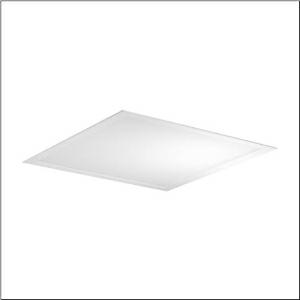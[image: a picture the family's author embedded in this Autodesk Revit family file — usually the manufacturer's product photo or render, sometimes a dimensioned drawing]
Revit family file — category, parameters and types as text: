
# Revit family: apollon_21_square_51mq11wc2454
name_source: partatom
category: Lighting Fixtures
units: mm (PartAtom-declared; Revit-internal decimal feet)

## family parameters
Cut with Voids When Loaded = No
Host = Face
Light Source = No
Part Type = Normal
Room Calculation Point = No
Round Connector Dimension = Use Diameter
Shared = No

## types (1)
- Apollon 21 square (1 x LED, 4200 lm, 24.7 W, 4000K)
    Apparent Load = 25 VA
    CIE Flux Codes = 60 87 97 100 100
    Color Rendering = 80
    Color Temperature = 4000K
    Default Elevation = 1800 mm
    Description = Apollon 21 square, office luminaire, primary optical cover: micro prismatic cover, of PMMA, CAT 2 (L<= 3000cd/m²), light emission: direct distribution, primary light characteristic: symmetric, installation type: lay-in mounting, recessed, LED, rated luminous flux: 4.200lm, luminous efficacy: 170lm/W, light colour: 840, colour temperature: 4000K, control gear: DALI 2, Multilumen, with terminal, 5-pole, mains connection: 220..240V, AC/DC, 0/50..60Hz, rated input power: 24.7W, suitable for self-contained emergency lighting element 59MQE002602A with integrated self-test function according to EN 60598-2-22, housing, of aluminium, coated, traffic white (RAL 9016), module: M625, length: 620mm, width: 620mm, height: 55mm, housing upper side, of sheet steel, galvanised, protection rating (complete): IP20, protection rating (lamp compartment, on room side): IP54, insulation class (complete): insulation class II (safety insulation), certification: CE, ENEC, UKCA, impact resistance: IK03, permissible operating ambient temperature: -20..+45°C, standard: EN 60598-2-22, corresponds to IFS (International Featured Standards) requirements for safety and quality in the food industry, packaging unit: 1 piece
    Height = 0 mm  [stored 0 ft]
    Lamp = 1 x LED
    Lamp Light Flux = 4200 lm
    Lamp Power = 24.7 W
    Lamp count = 1
    Length = 620 mm
    Luminous efficacy = 170 lm/W
    Manufacturer = Siteco
    ModVariant = No
    Model = 51MQ11WC2454
    Mounting Place = Ceiling
    Mounting Type = Recessed
    Number of Poles = 1
    OnlyDefault = Yes
    Power Factor = 1
    Product Name = Apollon 21 square
    Product group = office luminaire | ceiling recessed
    ProductGroupID = 400
    Protection Class = Protection class II
    Protection Degree = IP 20
    RLX_Detail_Level = 1
    RLX_Emergency_Light_Flux = 0 lm
    RLX_Emergency_Type = 0
    RLX_Emergency_Type_DB = No
    RlxData = <blob elided: 13293 chars, md5=c075d8e3>
    Socket = socket
    Standby Power = 0 W
    System Light Flux = 4200 lm
    System Power = 25 W
    Type Comments = Product without accessories
    Type Image = l_1291054.jpg
    URL = http://relux.com
    VarID = ---
    Voltage = 0 V
    Weight = 0.00 kg
    Width = 620 mm

note: [stored X ft] marks values corroborated as IEEE doubles in the binary element streams (Revit-internal decimal feet)

## geometry (parser evidence)
native form markers: Sweep x11
no freeform markers — native parametric forms only
